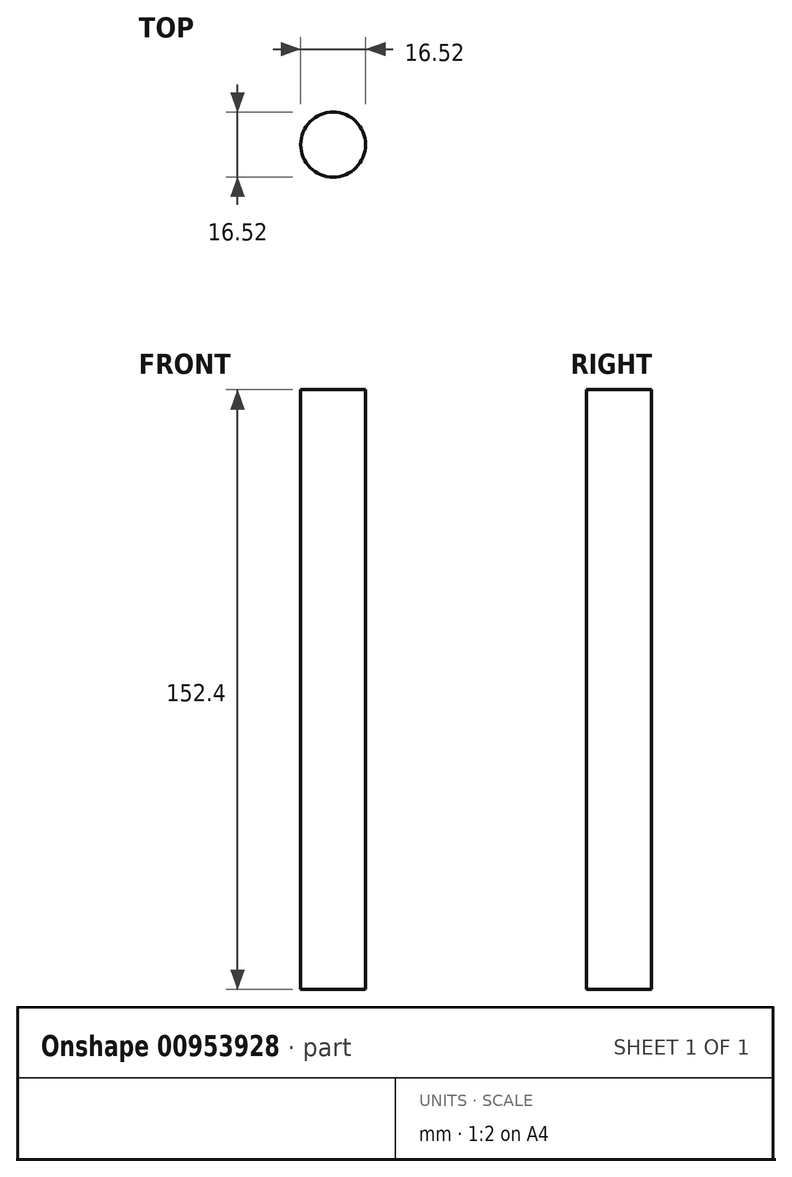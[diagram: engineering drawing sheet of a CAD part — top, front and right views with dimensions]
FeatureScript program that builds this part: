
annotation { "Feature Type Name" : "Feature", "Feature Type Description" : "" }
export const myFeature = defineFeature(function(context is Context, id is Id, definition is map)
    precondition{}
    {
        {
            var Q0;
            Q0=qCreatedBy(makeId("Top.planeOp"),FACE);
            var sketch = newSketch(context, id + "F0", { "sketchPlane" : qUnion([Q0])});
            skCircle(sketch, "E0", {"center": v(0, 0) * mm, "radius": 8.26 * mm});
            skSolve(sketch);
        }
        {
            var Q0;
            Q0 = qSketchRegion(id + "F0", true);
            extrude(context, id + "F1", {"entities" : qUnion([Q0]), "depth" : 152.4 * mm, "offsetDistance" : 25.4 * mm});
        }
    });
